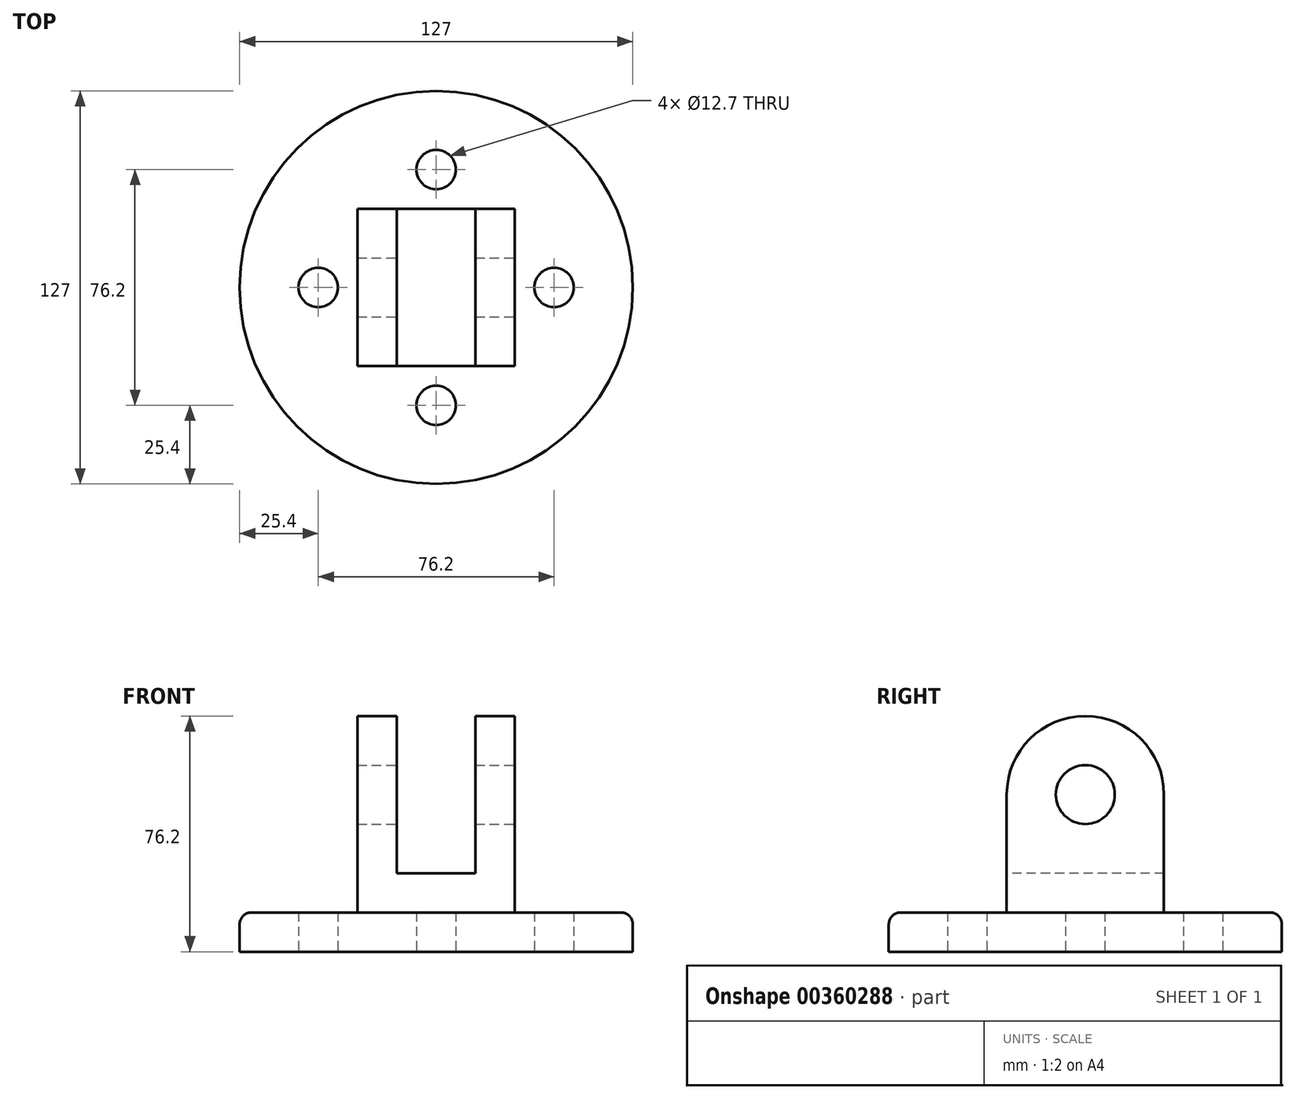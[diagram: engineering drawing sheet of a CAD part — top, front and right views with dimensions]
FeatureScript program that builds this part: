
annotation { "Feature Type Name" : "Feature", "Feature Type Description" : "" }
export const myFeature = defineFeature(function(context is Context, id is Id, definition is map)
    precondition{}
    {
        {
            var Q0;
            Q0=qCreatedBy(makeId("Top.planeOp"),FACE);
            var sketch = newSketch(context, id + "F0", { "sketchPlane" : qUnion([Q0])});
            skCircle(sketch, "E0", {"center": v(0, 0) * mm, "radius": 63.5 * mm});
            skArc(sketch, "E1", {"start": v(6.33, 37.57) * mm, "mid": v(0, 38.1) * mm, "end": v(-6.33, 37.57) * mm});
            skLineSegment(sketch, "E2", {"start": v(0, 0) * mm, "end": v(38.1, 0) * mm});
            skLineSegment(sketch, "E3", {"start": v(38.1, 0) * mm, "end": v(0, 0) * mm});
            skLineSegment(sketch, "E4", {"start": v(0, 38.1) * mm, "end": v(0, 0) * mm});
            skLineSegment(sketch, "E5", {"start": v(-38.1, 0) * mm, "end": v(0, 0) * mm});
            skCircle(sketch, "E6", {"center": v(0, 38.1) * mm, "radius": 6.35 * mm});
            skCircle(sketch, "E7", {"center": v(-38.1, 0) * mm, "radius": 6.35 * mm});
            skCircle(sketch, "E8", {"center": v(0, -38.1) * mm, "radius": 6.35 * mm});
            skCircle(sketch, "E9", {"center": v(38.1, 0) * mm, "radius": 6.35 * mm});
            skArc(sketch, "E10.trimOffspring", {"start": v(-37.57, 6.33) * mm, "mid": v(-38.1, 0) * mm, "end": v(-37.57, -6.33) * mm});
            skArc(sketch, "E11.trimOffspring", {"start": v(-6.33, -37.57) * mm, "mid": v(0, -38.1) * mm, "end": v(6.33, -37.57) * mm});
            skArc(sketch, "E12.trimOffspring", {"start": v(37.57, -6.33) * mm, "mid": v(38.1, 0) * mm, "end": v(37.57, 6.33) * mm});
            skSolve(sketch);
        }
        {
            var Q0;
            Q0 = qSketchRegion(id + "F0", true);
            extrude(context, id + "F1", {"entities" : qUnion([Q0]), "depth" : 12.7 * mm});
        }
        {
            var Q0;
            Q0=makeQuery(id+"F1.opExtrude","CAP_FACE",FACE,{"disambiguationData":[OSD([sQuery(id+"F0.wireOp",EDGE,"E0"),sQuery(id+"F0.wireOp",EDGE,"E6"),sQuery(id+"F0.wireOp",EDGE,"E7"),sQuery(id+"F0.wireOp",EDGE,"E8"),sQuery(id+"F0.wireOp",EDGE,"E9")])],"isStart":false});
            var sketch = newSketch(context, id + "F2", { "sketchPlane" : qUnion([Q0])});
            skLineSegment(sketch, "E13", {"start": v(0, 0) * mm, "end": v(0, 25.4) * mm});
            skLineSegment(sketch, "E14", {"start": v(0, 25.4) * mm, "end": v(-25.4, 25.4) * mm});
            skLineSegment(sketch, "E15", {"start": v(-25.4, 25.4) * mm, "end": v(-25.4, -25.4) * mm});
            skLineSegment(sketch, "E16", {"start": v(-25.4, -25.4) * mm, "end": v(25.4, -25.4) * mm});
            skLineSegment(sketch, "E17", {"start": v(25.4, -25.4) * mm, "end": v(25.4, 25.4) * mm});
            skLineSegment(sketch, "E18", {"start": v(25.4, 25.4) * mm, "end": v(0, 25.4) * mm});
            skSolve(sketch);
        }
        {
            var Q0;
            Q0 = qSketchRegion(id + "F2", true);
            extrude(context, id + "F3", {"entities" : qUnion([Q0]), "operationType" : NewBodyOperationType.ADD, "depth" : 63.5 * mm});
        }
        {
            var Q0;
            Q0=makeQuery(id+"F3.opExtrude","SWEPT_FACE",FACE,{"disambiguationData":[OSD([sQuery(id+"F2.wireOp",EDGE,"E16")])]});
            var sketch = newSketch(context, id + "F4", { "sketchPlane" : qUnion([Q0])});
            skLineSegment(sketch, "E19", {"start": v(-25.4, 76.2) * mm, "end": v(-12.7, 76.2) * mm});
            skLineSegment(sketch, "E20", {"start": v(-12.7, 76.2) * mm, "end": v(-12.7, 25.4) * mm});
            skLineSegment(sketch, "E21", {"start": v(-12.7, 25.4) * mm, "end": v(12.7, 25.4) * mm});
            skLineSegment(sketch, "E22", {"start": v(12.7, 25.4) * mm, "end": v(12.7, 76.2) * mm});
            skLineSegment(sketch, "E23", {"start": v(12.7, 76.2) * mm, "end": v(-12.7, 76.2) * mm});
            skSolve(sketch);
        }
        {
            var Q0;
            Q0 = qSketchRegion(id + "F4", true);
            extrude(context, id + "F5", {"entities" : qUnion([Q0]), "operationType" : NewBodyOperationType.REMOVE, "oppositeDirection" : true, "depth" : 50.8 * mm});
        }
        {
            var Q0;
            Q0=makeQuery(id+"F3.opExtrude","SWEPT_FACE",FACE,{"disambiguationData":[OSD([sQuery(id+"F2.wireOp",EDGE,"E17")])]});
            var sketch = newSketch(context, id + "F6", { "sketchPlane" : qUnion([Q0])});
            skLineSegment(sketch, "E24", {"start": v(-25.4, 76.2) * mm, "end": v(0, 76.2) * mm});
            skLineSegment(sketch, "E25", {"start": v(0, 76.2) * mm, "end": v(0, 0) * mm});
            skLineSegment(sketch, "E26", {"start": v(0, 50.8) * mm, "end": v(0, 0) * mm});
            skCircle(sketch, "E27", {"center": v(0, 50.8) * mm, "radius": 9.53 * mm});
            skSolve(sketch);
        }
        {
            var Q0;
            Q0 = qSketchRegion(id + "F6", true);
            extrude(context, id + "F7", {"entities" : qUnion([Q0]), "operationType" : NewBodyOperationType.REMOVE, "oppositeDirection" : true, "depth" : 127 * mm});
        }
        {
            var Q0;
            {var subQ0=sQuery(id+"F2.wireOp",EDGE,"E17");var subQ1=sQuery(id+"F2.wireOp",EDGE,"E16");Q0=makeQuery(id+"F5.boolean.opBoolean","SPLIT",EDGE,{"disambiguationData":[TD([makeQuery(id+"F3.opExtrude","SWEPT_FACE",FACE,{"disambiguationData":[OSD([subQ0])]})])],"derivedFrom":makeQuery(id+"F3.opExtrude","CAP_EDGE",EDGE,{"disambiguationData":[OSD([subQ1])],"isStart":false})});}
            var Q1;
            {var subQ0=sQuery(id+"F2.wireOp",EDGE,"E18");var subQ1=sQuery(id+"F2.wireOp",EDGE,"E17");var subQ2=sQuery(id+"F2.wireOp",EDGE,"E14");Q1=makeQuery(id+"F5.boolean.opBoolean","SPLIT",EDGE,{"disambiguationData":[TD([makeQuery(id+"F3.opExtrude","SWEPT_FACE",FACE,{"disambiguationData":[OSD([subQ1])]})])],"derivedFrom":makeQuery(id+"F3.opExtrude","CAP_EDGE",EDGE,{"disambiguationData":[OSD([subQ2,subQ0])],"isStart":false})});}
            var Q2;
            {var subQ0=sQuery(id+"F2.wireOp",EDGE,"E16");var subQ1=sQuery(id+"F2.wireOp",EDGE,"E15");Q2=makeQuery(id+"F5.boolean.opBoolean","SPLIT",EDGE,{"disambiguationData":[TD([makeQuery(id+"F3.opExtrude","SWEPT_FACE",FACE,{"disambiguationData":[OSD([subQ1])]})])],"derivedFrom":makeQuery(id+"F3.opExtrude","CAP_EDGE",EDGE,{"disambiguationData":[OSD([subQ0])],"isStart":false})});}
            var Q3;
            {var subQ0=sQuery(id+"F2.wireOp",EDGE,"E18");var subQ1=sQuery(id+"F2.wireOp",EDGE,"E15");var subQ2=sQuery(id+"F2.wireOp",EDGE,"E14");Q3=makeQuery(id+"F5.boolean.opBoolean","SPLIT",EDGE,{"disambiguationData":[TD([makeQuery(id+"F3.opExtrude","SWEPT_FACE",FACE,{"disambiguationData":[OSD([subQ1])]})])],"derivedFrom":makeQuery(id+"F3.opExtrude","CAP_EDGE",EDGE,{"disambiguationData":[OSD([subQ2,subQ0])],"isStart":false})});}
            fillet(context, id + "F8", {"entities" : qUnion([Q0, Q1, Q2, Q3]), "radius" : 25.4 * mm, "tangentPropagation" : true, "allowEdgeOverflow" : false});
        }
        {
            var Q0;
            Q0=makeQuery(id+"F1.opExtrude","CAP_EDGE",EDGE,{"disambiguationData":[OSD([sQuery(id+"F0.wireOp",EDGE,"E0")])],"isStart":false});
            var Q1;
            Q1=makeQuery(id+"F3.opExtrude","CAP_EDGE",EDGE,{"disambiguationData":[OSD([sQuery(id+"F2.wireOp",EDGE,"E17")])],"isStart":true});
            var Q2;
            Q2=makeQuery(id+"F3.opExtrude","CAP_EDGE",EDGE,{"disambiguationData":[OSD([sQuery(id+"F2.wireOp",EDGE,"E16")])],"isStart":true});
            var Q3;
            Q3=makeQuery(id+"F3.opExtrude","CAP_EDGE",EDGE,{"disambiguationData":[OSD([sQuery(id+"F2.wireOp",EDGE,"E14"),sQuery(id+"F2.wireOp",EDGE,"E18")])],"isStart":true});
            var Q4;
            Q4=makeQuery(id+"F3.opExtrude","CAP_EDGE",EDGE,{"disambiguationData":[OSD([sQuery(id+"F2.wireOp",EDGE,"E15")])],"isStart":true});
            fillet(context, id + "F9", {"entities" : qUnion([Q0, Q1, Q2, Q3, Q4]), "radius" : 3.8 * mm, "tangentPropagation" : true, "allowEdgeOverflow" : false});
        }
    });
